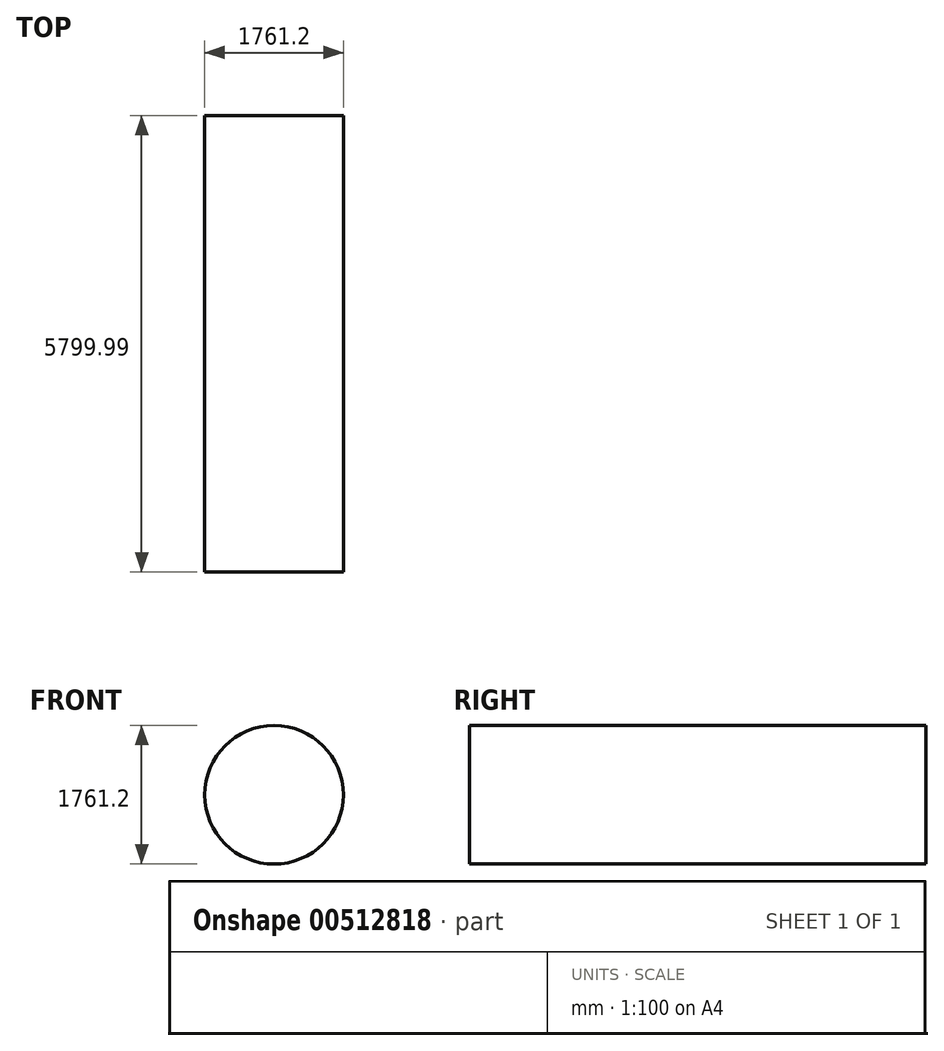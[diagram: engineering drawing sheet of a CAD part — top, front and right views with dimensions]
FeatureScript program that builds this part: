
annotation { "Feature Type Name" : "Feature", "Feature Type Description" : "" }
export const myFeature = defineFeature(function(context is Context, id is Id, definition is map)
    precondition{}
    {
        {
            var Q0;
            Q0=qCreatedBy(makeId("Front.planeOp"),FACE);
            var sketch = newSketch(context, id + "F0", { "sketchPlane" : qUnion([Q0])});
            skCircle(sketch, "E0", {"center": v(-8.63, 20.43) * mm, "radius": 880.6 * mm});
            skSolve(sketch);
        }
        {
            var Q0;
            Q0=makeQuery(id+"F0.imprint","IMPRINT",FACE,{"disambiguationData":[TD([[makeQuery(id+"F0.imprint","IMPRINT",EDGE,{"derivedFrom":sQuery(id+"F0.wireOp",EDGE,"E0")}),1.0]])]});
            var Q1;
            Q1=sQuery(id+"F0.wireOp",EDGE,"E0");
            extrude(context, id + "F1", {"entities" : qUnion([Q0]), "bodyType" : ToolBodyType.SURFACE, "surfaceEntities" : qUnion([Q1]), "depth" : 5799.99 * mm});
        }
    });
